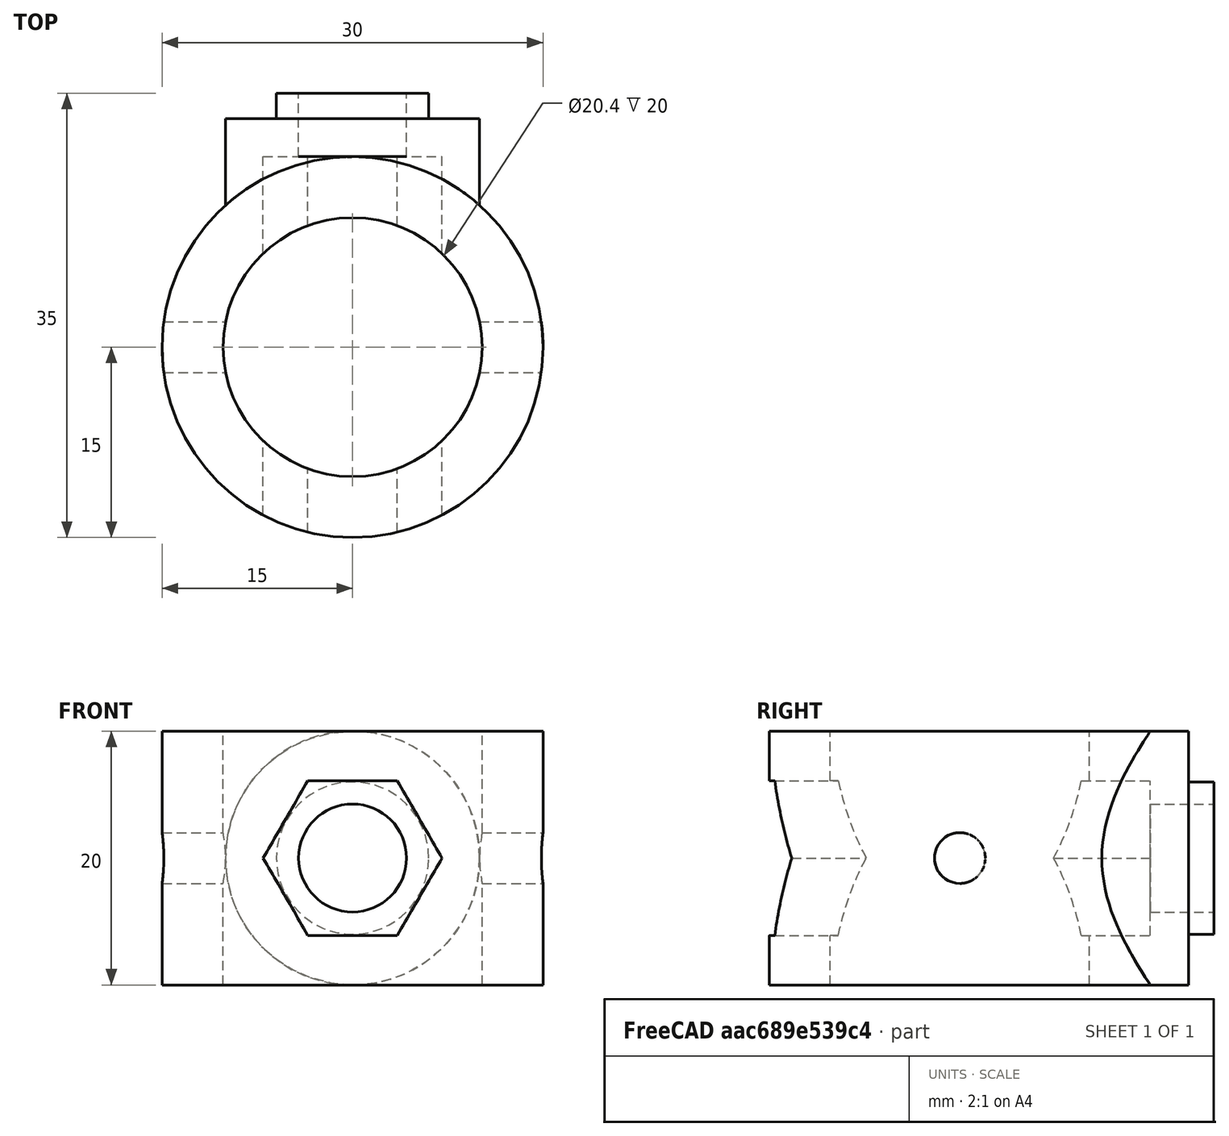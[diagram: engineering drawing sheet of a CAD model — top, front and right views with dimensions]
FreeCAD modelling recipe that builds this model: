
FCSTD DOCUMENT  (FreeCAD 0.18R16110 (Git))
Label: BaseWheelHolder
License: All rights reserved
LicenseURL: http://en.wikipedia.org/wiki/All_rights_reserved
objects: Part::Cylinder×6, Part::MultiFuse×2, Sketcher::SketchObject×1, PartDesign::Pad×1, PartDesign::Body×1, Part::Cut×1
note: 13 computed .brp shape members not serialized (recipe doc carries the construction recipe); baked Part::Feature solids carry a one-line shape summary decoded from their .brp

FEATURE [Part::Cylinder] Cylinder
  Angle = 360
  AttacherType = Attacher::AttachEngine3D
  Height = 20
  Placement = pos=(0,0,-10) rot=(0,0,1;0rad)
  Radius = 15
FEATURE [Part::Cylinder] Cylinder001
  Angle = 360
  AttacherType = Attacher::AttachEngine3D
  Height = 20
  Placement = pos=(0,0,-10) rot=(0,0,1;0rad)
  Radius = 10.2
FEATURE [Sketcher::SketchObject] Sketch
  MapMode = 5
  Placement = pos=(0,0,0) rot=(1,0,0;1.5708rad)
  Support = -> [XZ_Plane]
  sketch-geometry (7):
    g0: LineSegment StartX=3.52184 StartY=-6.1 StartZ=0 EndX=7.04367 EndY=0 EndZ=0
    g1: LineSegment StartX=7.04367 StartY=0 StartZ=0 EndX=3.52184 EndY=6.1 EndZ=0
    g2: LineSegment StartX=3.52184 StartY=6.1 StartZ=0 EndX=-3.52184 EndY=6.1 EndZ=0
    g3: LineSegment StartX=-3.52184 StartY=6.1 StartZ=0 EndX=-7.04367 EndY=0 EndZ=0
    g4: LineSegment StartX=-7.04367 StartY=0 StartZ=0 EndX=-3.52184 EndY=-6.1 EndZ=0
    g5: LineSegment StartX=-3.52184 StartY=-6.1 StartZ=0 EndX=3.52184 EndY=-6.1 EndZ=0
    g6: Circle [constr] CenterX=0 CenterY=0 CenterZ=0 NormalX=0 NormalY=0 NormalZ=1 AngleXU=0 Radius=7.04367
  constraints (16):
    c: Coincident(g0,g1)
    c: Coincident(g1,g2)
    c: Coincident(g2,g3)
    c: Coincident(g3,g4)
    c: Coincident(g4,g5)
    c: Coincident(g5,g0)
    c: Equal(g0, g1-g5) x5
    c: PointOnObject(g0,g6)
    c: PointOnObject(g1,g6)
    c: PointOnObject(g2,g6)
    c: PointOnObject(g3,g6)
    c: PointOnObject(g4,g6)
    c: PointOnObject(g5,g6)
    c: Coincident(g-1,g6)
    c: DistanceY(g0,g1) = 12.2
    c: DistanceY(g4,g0) = 0
FEATURE [PartDesign::Pad] Pad
  Length = 30
  Length2 = 100
  Placement = pos=(0,0,0) rot=(1,0,0;1.5708rad)
  Profile = -> Sketch
  Reversed = true
  Type = 0
FEATURE [PartDesign::Body] Body
  Group = -> [Sketch,Pad]
  Origin = -> Origin
  Placement = pos=(0,-15,0) rot=(0,0,1;0rad)
  Tip = -> Pad
FEATURE [Part::Cylinder] Cylinder002
  Angle = 360
  AttacherType = Attacher::AttachEngine3D
  Height = 10
  Placement = pos=(0,10,-2e-15) rot=(-1,0,0;1.5708rad)
  Radius = 4.25
FEATURE [Part::Cylinder] Cylinder003
  Angle = 360
  AttacherType = Attacher::AttachEngine3D
  Height = 8
  Placement = pos=(0,10,-2e-15) rot=(-1,0,0;1.5708rad)
  Radius = 10
FEATURE [Part::Cylinder] Cylinder004
  Angle = 360
  AttacherType = Attacher::AttachEngine3D
  Height = 2
  Placement = pos=(0,18,-4e-15) rot=(-1,0,0;1.5708rad)
  Radius = 6
FEATURE [Part::MultiFuse] Fusion001  label="Positive Fusion"
  Shapes = -> [Cylinder,Cylinder003,Cylinder004]
FEATURE [Part::Cylinder] Cylinder005
  Angle = 360
  AttacherType = Attacher::AttachEngine3D
  Height = 30
  Placement = pos=(-15,0,-3e-15) rot=(0,1,0;1.5708rad)
  Radius = 2
FEATURE [Part::MultiFuse] Fusion  label="Negative Fusion"
  Shapes = -> [Body,Cylinder001,Cylinder002,Cylinder005]
FEATURE [Part::Cut] Cut
  Base = -> Fusion001
  Tool = -> Fusion
